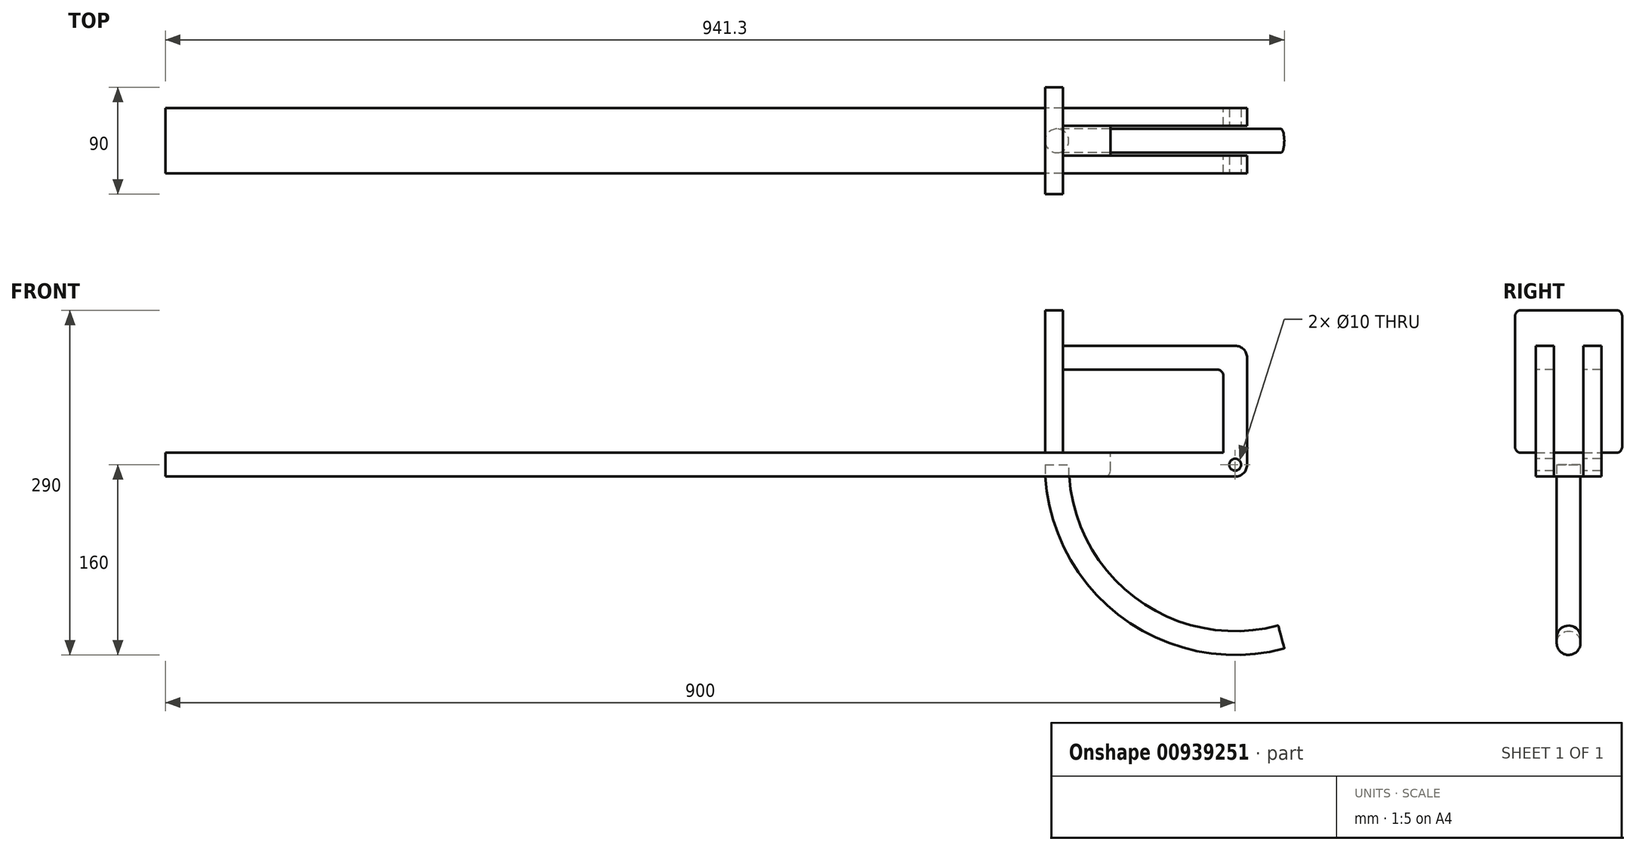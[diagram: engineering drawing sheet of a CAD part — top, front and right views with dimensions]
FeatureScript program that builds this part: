
annotation { "Feature Type Name" : "Feature", "Feature Type Description" : "" }
export const myFeature = defineFeature(function(context is Context, id is Id, definition is map)
    precondition{}
    {
        {
            var Q0;
            Q0=qCreatedBy(makeId("Front.planeOp"),FACE);
            var sketch = newSketch(context, id + "F0", { "sketchPlane" : qUnion([Q0])});
            skCircle(sketch, "E0", {"center": v(0, 0) * mm, "radius": 5 * mm});
            skArc(sketch, "E1", {"start": v(0, -10) * mm, "mid": v(10, 0) * mm, "end": v(0, 10) * mm});
            skLineSegment(sketch, "E2", {"start": v(0, 10) * mm, "end": v(-900, 10) * mm});
            skLineSegment(sketch, "E3", {"start": v(0, -10) * mm, "end": v(-900, -10) * mm});
            skLineSegment(sketch, "E4", {"start": v(-900, -10) * mm, "end": v(-900, 10) * mm});
            skSolve(sketch);
        }
        {
            var Q0;
            Q0=makeQuery(id+"F0.imprint","IMPRINT",FACE,{"disambiguationData":[TD([[makeQuery(id+"F0.imprint","IMPRINT",EDGE,{"derivedFrom":sQuery(id+"F0.wireOp",EDGE,"E0")}),-1.0]])]});
            extrude(context, id + "F1", {"entities" : qUnion([Q0]), "oppositeDirection" : true, "depth" : 27.5 * mm, "offsetDistance" : 25 * mm, "hasSecondDirection" : true, "secondDirectionOppositeDirection" : false, "secondDirectionDepth" : 27.5 * mm});
        }
        {
            var Q0;
            Q0=makeQuery(id+"F1.opExtrude","CAP_FACE",FACE,{"disambiguationData":[OSD([sQuery(id+"F0.wireOp",EDGE,"E0"),sQuery(id+"F0.wireOp",EDGE,"E1"),sQuery(id+"F0.wireOp",EDGE,"E2"),sQuery(id+"F0.wireOp",EDGE,"E3"),sQuery(id+"F0.wireOp",EDGE,"E4")])],"isStart":true});
            cPlane(context, id + "F2", {"entities" : qUnion([Q0]), "cplaneType" : CPlaneType.OFFSET, "offset" : 27.5 * mm, "oppositeDirection" : true, "width" : 150 * mm, "height" : 150 * mm});
        }
        {
            var Q0;
            Q0=makeQuery(id+"F1.opExtrude","CAP_FACE",FACE,{"disambiguationData":[OSD([sQuery(id+"F0.wireOp",EDGE,"E0"),sQuery(id+"F0.wireOp",EDGE,"E1"),sQuery(id+"F0.wireOp",EDGE,"E2"),sQuery(id+"F0.wireOp",EDGE,"E3"),sQuery(id+"F0.wireOp",EDGE,"E4")])],"isStart":true});
            cPlane(context, id + "F3", {"entities" : qUnion([Q0]), "cplaneType" : CPlaneType.OFFSET, "offset" : 0 * mm, "width" : 150 * mm, "height" : 150 * mm});
        }
        {
            var Q0;
            Q0=qCreatedBy(id+"F3.planeOp",FACE);
            var sketch = newSketch(context, id + "F4", { "sketchPlane" : qUnion([Q0])});
            skArc(sketch, "E5", {"start": v(-10, 0) * mm, "mid": v(0, -10) * mm, "end": v(10, 0) * mm});
            skLineSegment(sketch, "E6", {"start": v(10, 0) * mm, "end": v(10, 90) * mm});
            skArc(sketch, "E7", {"start": v(10, 90) * mm, "mid": v(7.07, 97.07) * mm, "end": v(0, 100) * mm});
            skLineSegment(sketch, "E8", {"start": v(0, 100) * mm, "end": v(-145, 100) * mm});
            skLineSegment(sketch, "E9", {"start": v(-145, 100) * mm, "end": v(-145, 80) * mm});
            skLineSegment(sketch, "E10", {"start": v(-145, 80) * mm, "end": v(-10, 80) * mm});
            skLineSegment(sketch, "E11", {"start": v(-10, 0) * mm, "end": v(-10, 80) * mm});
            skLineSegment(sketch, "E12", {"start": v(-145, 80) * mm, "end": v(-145, 10) * mm});
            skPoint(sketch, "E13.orphan", {"position": v(0, 80) * mm});
            skCircle(sketch, "E14", {"center": v(0, 0) * mm, "radius": 5 * mm});
            skSolve(sketch);
        }
        {
            var Q0;
            Q0=makeQuery(id+"F4.imprint","IMPRINT",FACE,{"disambiguationData":[TD([[makeQuery(id+"F4.imprint","IMPRINT",EDGE,{"derivedFrom":sQuery(id+"F4.wireOp",EDGE,"E5")}),1.0]])]});
            extrude(context, id + "F5", {"entities" : qUnion([Q0]), "operationType" : NewBodyOperationType.ADD, "oppositeDirection" : true, "depth" : 55 * mm, "offsetDistance" : 25 * mm});
        }
        {
            var Q0;
            Q0=qCreatedBy(id+"F2.planeOp",FACE);
            var sketch = newSketch(context, id + "F6", { "sketchPlane" : qUnion([Q0])});
            skLineSegment(sketch, "E15", {"start": v(30, -42.08) * mm, "end": v(30, 107.92) * mm});
            skLineSegment(sketch, "E16", {"start": v(30, 107.92) * mm, "end": v(-145, 107.92) * mm});
            skLineSegment(sketch, "E17", {"start": v(-145, 107.92) * mm, "end": v(-145, 27.92) * mm});
            skLineSegment(sketch, "E18", {"start": v(30, -42.08) * mm, "end": v(-105, -42.08) * mm});
            skLineSegment(sketch, "E19", {"start": v(-105, -42.08) * mm, "end": v(-105, 28.37) * mm});
            skLineSegment(sketch, "E20", {"start": v(-105, 28.37) * mm, "end": v(-145, 27.92) * mm});
            skSolve(sketch);
        }
        {
            var Q0;
            Q0=makeQuery(id+"F6.imprint","IMPRINT",FACE,{"disambiguationData":[TD([[makeQuery(id+"F6.imprint","IMPRINT",EDGE,{"derivedFrom":sQuery(id+"F6.wireOp",EDGE,"E15")}),1.0]])]});
            extrude(context, id + "F7", {"entities" : qUnion([Q0]), "operationType" : NewBodyOperationType.REMOVE, "oppositeDirection" : true, "depth" : 12.5 * mm, "offsetDistance" : 25 * mm, "hasSecondDirection" : true, "secondDirectionOppositeDirection" : false, "secondDirectionDepth" : 12.5 * mm});
        }
        {
            var Q0;
            Q0=qCreatedBy(id+"F2.planeOp",FACE);
            var sketch = newSketch(context, id + "F8", { "sketchPlane" : qUnion([Q0])});
            skArc(sketch, "E21", {"start": v(-150, 0) * mm, "mid": v(-91.31, -119) * mm, "end": v(38.82, -144.89) * mm});
            skSolve(sketch);
        }
        {
            var Q0;
            Q0=qCreatedBy(id+"F2.planeOp",FACE);
            var sketch = newSketch(context, id + "F9", { "sketchPlane" : qUnion([Q0])});
            skLineSegment(sketch, "E22", {"start": v(0, 0) * mm, "end": v(0, 10) * mm});
            skLineSegment(sketch, "E23", {"start": v(0, 10) * mm, "end": v(-145, 10) * mm});
            skLineSegment(sketch, "E24", {"start": v(-145, 10) * mm, "end": v(-145, 130) * mm});
            skLineSegment(sketch, "E25", {"start": v(-145, 130) * mm, "end": v(-160, 130) * mm});
            skLineSegment(sketch, "E26", {"start": v(-160, 130) * mm, "end": v(-160, 10) * mm});
            skLineSegment(sketch, "E27", {"start": v(-160, 10) * mm, "end": v(-145, 10) * mm});
            skSolve(sketch);
        }
        {
            var Q0;
            Q0=makeQuery(id+"F9.imprint","IMPRINT",FACE,{"disambiguationData":[TD([[makeQuery(id+"F9.imprint","IMPRINT",EDGE,{"derivedFrom":sQuery(id+"F9.wireOp",EDGE,"E24")}),1.0]])]});
            extrude(context, id + "F10", {"entities" : qUnion([Q0]), "operationType" : NewBodyOperationType.ADD, "depth" : 45 * mm, "offsetDistance" : 25 * mm, "hasSecondDirection" : true, "secondDirectionOppositeDirection" : true, "secondDirectionDepth" : 45 * mm});
        }
        {
            var Q0;
            Q0=makeQuery(id+"F10.opExtrude","CAP_EDGE",EDGE,{"disambiguationData":[OSD([sQuery(id+"F9.wireOp",EDGE,"E25")])],"isStart":false});
            var Q1;
            Q1=makeQuery(id+"F10.opExtrude","CAP_EDGE",EDGE,{"disambiguationData":[OSD([sQuery(id+"F9.wireOp",EDGE,"E25")])],"isStart":true});
            var Q2;
            Q2=makeQuery(id+"F10.opExtrude","CAP_EDGE",EDGE,{"disambiguationData":[OSD([sQuery(id+"F9.wireOp",EDGE,"E27")])],"isStart":false});
            var Q3;
            Q3=makeQuery(id+"F10.opExtrude","CAP_EDGE",EDGE,{"disambiguationData":[OSD([sQuery(id+"F9.wireOp",EDGE,"E27")])],"isStart":true});
            fillet(context, id + "F11", {"entities" : qUnion([Q0, Q1, Q2, Q3]), "radius" : 5 * mm, "tangentPropagation" : true, "allowEdgeOverflow" : false});
        }
        {
            var Q0;
            {var subQ0=sQuery(id+"F4.wireOp",EDGE,"E11");var subQ1=sQuery(id+"F4.wireOp",EDGE,"E10");Q0=makeQuery(id+"F7.boolean.opBoolean","SPLIT",EDGE,{"disambiguationData":[TD([makeQuery(id+"F7.opExtrude","CAP_FACE",FACE,{"disambiguationData":[OSD([sQuery(id+"F6.wireOp",EDGE,"E15"),sQuery(id+"F6.wireOp",EDGE,"E16"),sQuery(id+"F6.wireOp",EDGE,"E17"),sQuery(id+"F6.wireOp",EDGE,"0AUqPSAk-ax5Y-H1Up-l1sM-Z7PxQlakLnhN")])],"isStart":true})])],"derivedFrom":makeQuery(id+"F5.opExtrude","SWEPT_EDGE",EDGE,{"disambiguationData":[OSD([subQ1,subQ0])]})});}
            var Q1;
            {var subQ0=sQuery(id+"F4.wireOp",EDGE,"E11");var subQ1=sQuery(id+"F4.wireOp",EDGE,"E10");Q1=makeQuery(id+"F7.boolean.opBoolean","SPLIT",EDGE,{"disambiguationData":[TD([makeQuery(id+"F7.opExtrude","CAP_FACE",FACE,{"disambiguationData":[OSD([sQuery(id+"F6.wireOp",EDGE,"E15"),sQuery(id+"F6.wireOp",EDGE,"E16"),sQuery(id+"F6.wireOp",EDGE,"E17"),sQuery(id+"F6.wireOp",EDGE,"0AUqPSAk-ax5Y-H1Up-l1sM-Z7PxQlakLnhN")])],"isStart":false})])],"derivedFrom":makeQuery(id+"F5.opExtrude","SWEPT_EDGE",EDGE,{"disambiguationData":[OSD([subQ1,subQ0])]})});}
            fillet(context, id + "F12", {"entities" : qUnion([Q0, Q1]), "radius" : 5 * mm, "tangentPropagation" : true, "allowEdgeOverflow" : false});
        }
        {
            var Q0;
            Q0=makeQuery(id+"F1.opExtrude","SWEPT_FACE",FACE,{"disambiguationData":[OSD([sQuery(id+"F0.wireOp",EDGE,"E3")])]});
            cPlane(context, id + "F13", {"entities" : qUnion([Q0]), "cplaneType" : CPlaneType.OFFSET, "offset" : 10 * mm, "oppositeDirection" : true, "width" : 150 * mm, "height" : 150 * mm});
        }
        {
            var Q0;
            Q0=qCreatedBy(id+"F13.planeOp",FACE);
            var sketch = newSketch(context, id + "F14", { "sketchPlane" : qUnion([Q0])});
            skLineSegment(sketch, "E28", {"start": v(0, 0) * mm, "end": v(-150, 0) * mm});
            skCircle(sketch, "E29", {"center": v(-150, 0) * mm, "radius": 10 * mm});
            skSolve(sketch);
        }
        {
            var Q0;
            Q0=makeQuery(id+"F14.imprint","IMPRINT",FACE,{"disambiguationData":[TD([[makeQuery(id+"F14.imprint","IMPRINT",EDGE,{"derivedFrom":sQuery(id+"F14.wireOp",EDGE,"E29")}),1.0]])]});
            var Q1;
            Q1=sQuery(id+"F8.wireOp",EDGE,"E21");
            sweep(context, id + "F15", {"profiles" : qUnion([Q0]), "path" : qUnion([Q1])});
        }
        {
            var Q0;
            Q0=makeQuery(id+"F7.boolean.opBoolean","INTERSECT",EDGE,{"derivedFrom":[makeQuery(id+"F1.opExtrude","SWEPT_FACE",FACE,{"disambiguationData":[OSD([sQuery(id+"F0.wireOp",EDGE,"E3")])]}),makeQuery(id+"F7.opExtrude","SWEPT_FACE",FACE,{"disambiguationData":[OSD([sQuery(id+"F6.wireOp",EDGE,"E19")])]})]});
            fillet(context, id + "F16", {"entities" : qUnion([Q0]), "radius" : 5 * mm, "tangentPropagation" : true, "allowEdgeOverflow" : false});
        }
        {
            var Q0;
            Q0=makeQuery(id+"F15.opSweep","CAP_EDGE",EDGE,{"disambiguationData":[OSD([sQuery(id+"F8.wireOp",VERTEX,"E21.end"),sQuery(id+"F14.wireOp",EDGE,"E29")])],"isStart":false});
            fillet(context, id + "F17", {"entities" : qUnion([Q0]), "radius" : 0.5 * mm, "tangentPropagation" : true, "allowEdgeOverflow" : false});
        }
    });
